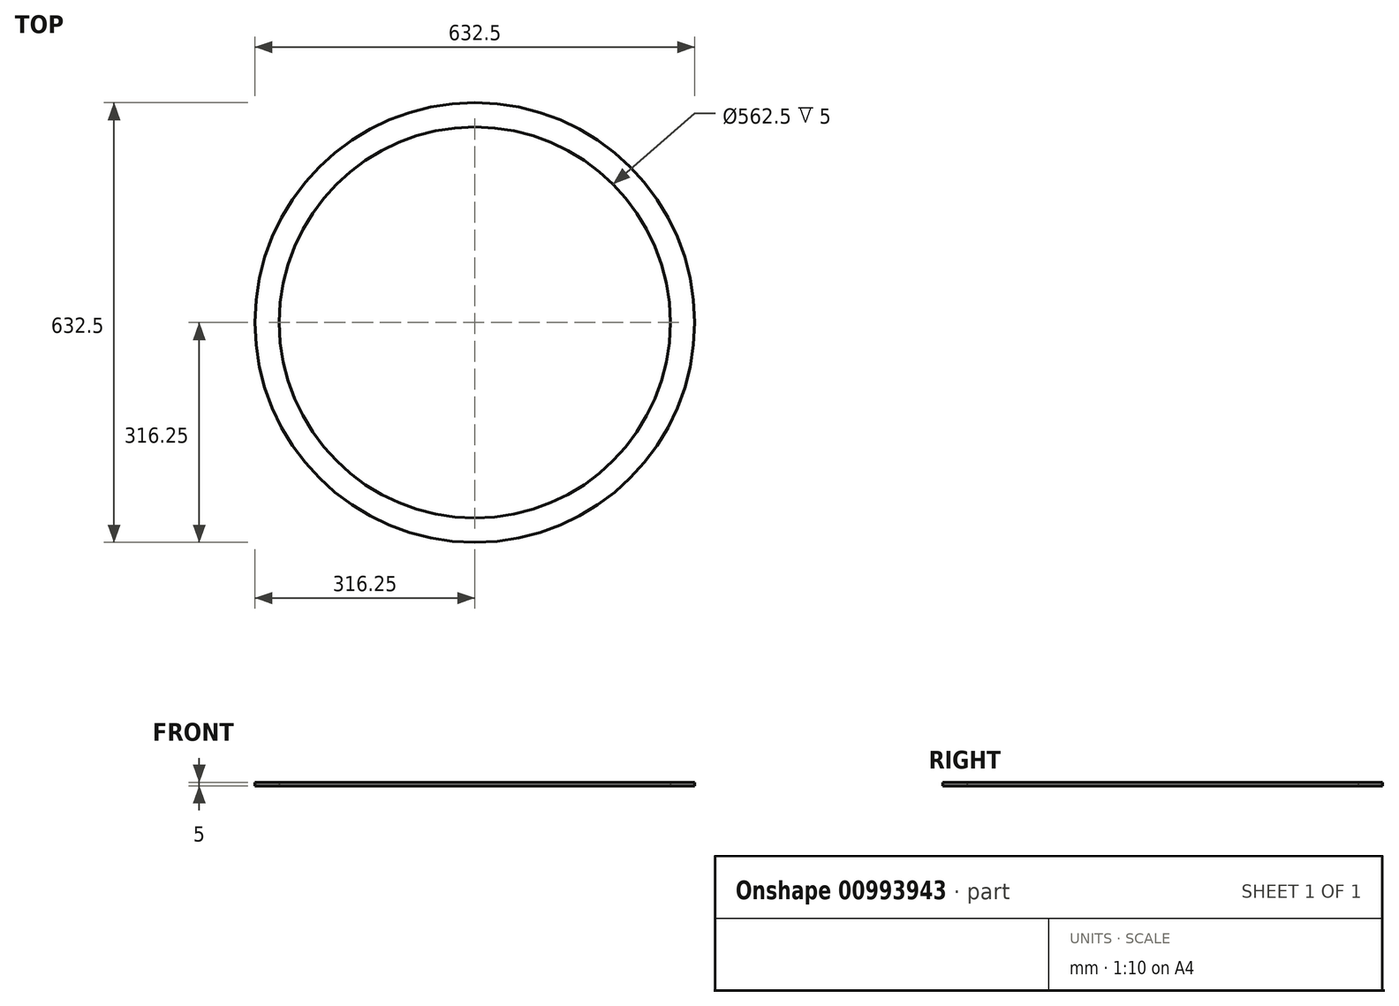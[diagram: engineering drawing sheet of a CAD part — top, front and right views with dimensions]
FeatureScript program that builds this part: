
annotation { "Feature Type Name" : "Feature", "Feature Type Description" : "" }
export const myFeature = defineFeature(function(context is Context, id is Id, definition is map)
    precondition{}
    {
        {
            var Q0;
            Q0=qCreatedBy(makeId("Top.planeOp"),FACE);
            var sketch = newSketch(context, id + "F0", { "sketchPlane" : qUnion([Q0])});
            skCircle(sketch, "E0", {"center": v(0, 0) * mm, "radius": 316.25 * mm});
            skCircle(sketch, "E1", {"center": v(0, 0) * mm, "radius": 281.25 * mm});
            skSolve(sketch);
        }
        {
            var Q0;
            Q0=makeQuery(id+"F0.imprint","IMPRINT",FACE,{"disambiguationData":[TD([[makeQuery(id+"F0.imprint","IMPRINT",EDGE,{"derivedFrom":sQuery(id+"F0.wireOp",EDGE,"E0")}),1.0]])]});
            extrude(context, id + "F1", {"entities" : qUnion([Q0]), "depth" : 5 * mm, "offsetDistance" : 25 * mm});
        }
    });
